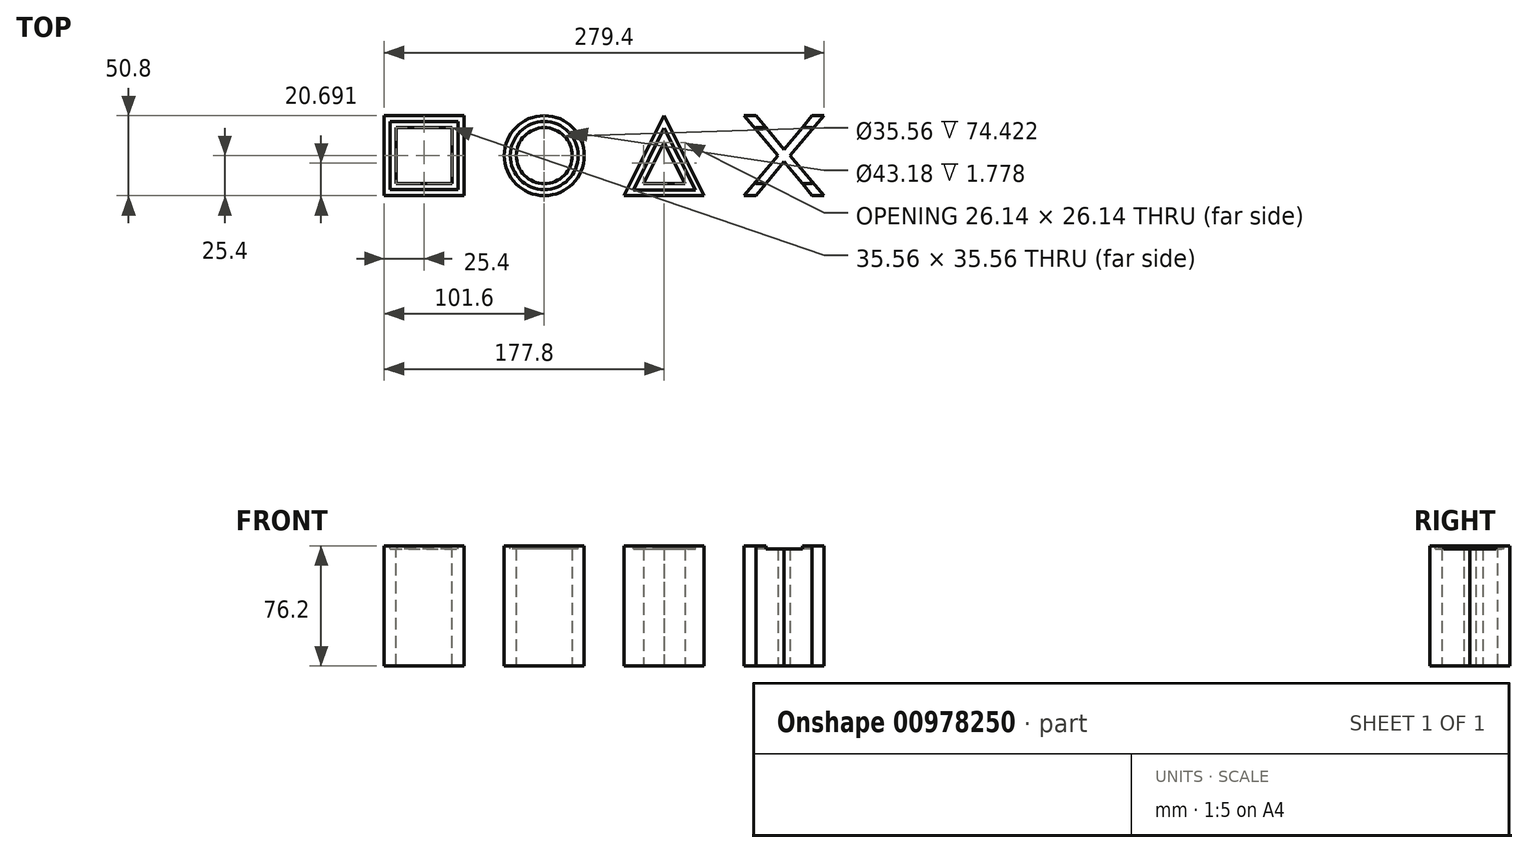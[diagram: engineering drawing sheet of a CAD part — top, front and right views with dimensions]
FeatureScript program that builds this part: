
annotation { "Feature Type Name" : "Feature", "Feature Type Description" : "" }
export const myFeature = defineFeature(function(context is Context, id is Id, definition is map)
    precondition{}
    {
        {
            var Q0;
            Q0=qCreatedBy(makeId("Top.planeOp"),FACE);
            var sketch = newSketch(context, id + "F0", { "sketchPlane" : qUnion([Q0])});
            skLineSegment(sketch, "E0.bottom", {"start": v(139.7, -25.4) * mm, "end": v(-139.7, -25.4) * mm});
            skLineSegment(sketch, "E0.top", {"start": v(139.7, 25.4) * mm, "end": v(-139.7, 25.4) * mm});
            skLineSegment(sketch, "E0.left", {"start": v(139.7, -25.4) * mm, "end": v(139.7, 25.4) * mm});
            skLineSegment(sketch, "E0.right", {"start": v(-139.7, -25.4) * mm, "end": v(-139.7, 25.4) * mm});
            skPoint(sketch, "E0.middle", {"position": v(0, 0) * mm});
            skSolve(sketch);
        }
        {
            var Q0;
            Q0=qSketchRegion(id+"F0",true);
            extrude(context, id + "F1", {"entities" : qUnion([Q0]), "oppositeDirection" : true, "depth" : 25.4 * mm, "offsetDistance" : 25.4 * mm});
        }
        {
            var Q0;
            Q0=makeQuery(id+"F1.opExtrude","CAP_FACE",FACE,{"disambiguationData":[OSD([sQuery(id+"F0.wireOp",EDGE,"E0.bottom"),sQuery(id+"F0.wireOp",EDGE,"E0.top"),sQuery(id+"F0.wireOp",EDGE,"E0.left"),sQuery(id+"F0.wireOp",EDGE,"E0.right")])],"isStart":true});
            var sketch = newSketch(context, id + "F2", { "sketchPlane" : qUnion([Q0])});
            skLineSegment(sketch, "E1.bottom", {"start": v(-139.7, 25.4) * mm, "end": v(-88.9, 25.4) * mm});
            skLineSegment(sketch, "E1.top", {"start": v(-139.7, -25.4) * mm, "end": v(-88.9, -25.4) * mm});
            skLineSegment(sketch, "E1.left", {"start": v(-139.7, 25.4) * mm, "end": v(-139.7, -25.4) * mm});
            skLineSegment(sketch, "E1.right", {"start": v(-88.9, 25.4) * mm, "end": v(-88.9, -25.4) * mm});
            skSolve(sketch);
        }
        {
            var Q0;
            Q0=qSketchRegion(id+"F2",true);
            extrude(context, id + "F3", {"entities" : qUnion([Q0]), "depth" : 127 * mm, "offsetDistance" : 25.4 * mm});
        }
        {
            var Q0;
            Q0=makeQuery(id+"F3.opExtrude","CAP_FACE",FACE,{"disambiguationData":[OSD([sQuery(id+"F2.wireOp",EDGE,"E1.bottom"),sQuery(id+"F2.wireOp",EDGE,"E1.top"),sQuery(id+"F2.wireOp",EDGE,"E1.left"),sQuery(id+"F2.wireOp",EDGE,"E1.right")])],"isStart":false});
            var sketch = newSketch(context, id + "F4", { "sketchPlane" : qUnion([Q0])});
            skLineSegment(sketch, "E2.bottom", {"start": v(-132.08, -17.78) * mm, "end": v(-96.52, -17.78) * mm});
            skLineSegment(sketch, "E2.top", {"start": v(-132.08, 17.78) * mm, "end": v(-96.52, 17.78) * mm});
            skLineSegment(sketch, "E2.left", {"start": v(-132.08, -17.78) * mm, "end": v(-132.08, 17.78) * mm});
            skLineSegment(sketch, "E2.right", {"start": v(-96.52, -17.78) * mm, "end": v(-96.52, 17.78) * mm});
            skPoint(sketch, "E2.middle", {"position": v(-114.3, 0) * mm});
            skPoint(sketch, "E2.middle.positionSnap0", {"position": v(-88.9, 0) * mm});
            skPoint(sketch, "E2.middle.positionSnap1", {"position": v(-114.3, 25.4) * mm});
            skPoint(sketch, "E2.centerSnap0", {"position": v(-88.9, 0) * mm});
            skPoint(sketch, "E2.centerSnap1", {"position": v(-114.3, 25.4) * mm});
            skSolve(sketch);
        }
        {
            var Q0;
            Q0=qSketchRegion(id+"F4",true);
            extrude(context, id + "F5", {"entities" : qUnion([Q0]), "operationType" : NewBodyOperationType.REMOVE, "oppositeDirection" : true, "depth" : 127 * mm, "offsetDistance" : 25.4 * mm});
        }
        {
            var Q0;
            Q0=makeQuery(id+"F1.opExtrude","CAP_FACE",FACE,{"disambiguationData":[OSD([sQuery(id+"F0.wireOp",EDGE,"E0.bottom"),sQuery(id+"F0.wireOp",EDGE,"E0.top"),sQuery(id+"F0.wireOp",EDGE,"E0.left"),sQuery(id+"F0.wireOp",EDGE,"E0.right")])],"isStart":true});
            var sketch = newSketch(context, id + "F6", { "sketchPlane" : qUnion([Q0])});
            skCircle(sketch, "E3", {"center": v(-38.1, 0) * mm, "radius": 25.4 * mm});
            skCircle(sketch, "E4", {"center": v(-38.1, 0) * mm, "radius": 17.78 * mm});
            skSolve(sketch);
        }
        {
            var Q0;
            Q0=qSketchRegion(id+"F6",true);
            extrude(context, id + "F7", {"entities" : qUnion([Q0]), "depth" : 127 * mm, "offsetDistance" : 25.4 * mm});
        }
        {
            var Q0;
            Q0=makeQuery(id+"F1.opExtrude","CAP_FACE",FACE,{"disambiguationData":[OSD([sQuery(id+"F0.wireOp",EDGE,"E0.bottom"),sQuery(id+"F0.wireOp",EDGE,"E0.top"),sQuery(id+"F0.wireOp",EDGE,"E0.left"),sQuery(id+"F0.wireOp",EDGE,"E0.right")])],"isStart":true});
            var sketch = newSketch(context, id + "F8", { "sketchPlane" : qUnion([Q0])});
            skLineSegment(sketch, "E5.bottom", {"start": v(12.7, -25.4) * mm, "end": v(63.5, -25.4) * mm});
            skLineSegment(sketch, "E6", {"start": v(38.1, 25.4) * mm, "end": v(12.7, -25.4) * mm});
            skLineSegment(sketch, "E7", {"start": v(38.1, 25.4) * mm, "end": v(63.5, -25.4) * mm});
            skLineSegment(sketch, "E8", {"start": v(38.1, 8.36) * mm, "end": v(25.03, -17.78) * mm});
            skLineSegment(sketch, "E9", {"start": v(25.03, -17.78) * mm, "end": v(51.17, -17.78) * mm});
            skLineSegment(sketch, "E10", {"start": v(51.17, -17.78) * mm, "end": v(38.1, 8.36) * mm});
            skSolve(sketch);
        }
        {
            var Q0;
            Q0=qSketchRegion(id+"F8",true);
            extrude(context, id + "F9", {"entities" : qUnion([Q0]), "depth" : 127 * mm, "offsetDistance" : 25.4 * mm});
        }
        {
            var Q0;
            Q0=makeQuery(id+"F1.opExtrude","CAP_FACE",FACE,{"disambiguationData":[OSD([sQuery(id+"F0.wireOp",EDGE,"E0.bottom"),sQuery(id+"F0.wireOp",EDGE,"E0.top"),sQuery(id+"F0.wireOp",EDGE,"E0.left"),sQuery(id+"F0.wireOp",EDGE,"E0.right")])],"isStart":true});
            var sketch = newSketch(context, id + "F10", { "sketchPlane" : qUnion([Q0])});
            skPoint(sketch, "E11.middle", {"position": v(114.3, 0) * mm});
            skLineSegment(sketch, "E12", {"start": v(88.9, -25.4) * mm, "end": v(96.52, -25.4) * mm});
            skLineSegment(sketch, "E13", {"start": v(96.52, -25.4) * mm, "end": v(114.3, -3.81) * mm});
            skLineSegment(sketch, "E14", {"start": v(88.9, -25.4) * mm, "end": v(110.49, 0) * mm});
            skLineSegment(sketch, "E15", {"start": v(110.49, 0) * mm, "end": v(88.9, 25.4) * mm});
            skLineSegment(sketch, "E16", {"start": v(88.9, 25.4) * mm, "end": v(96.52, 25.4) * mm});
            skLineSegment(sketch, "E17", {"start": v(96.52, 25.4) * mm, "end": v(114.3, 3.8) * mm});
            skLineSegment(sketch, "E18", {"start": v(139.7, 25.4) * mm, "end": v(118.11, 0) * mm});
            skLineSegment(sketch, "E19", {"start": v(118.1, 0) * mm, "end": v(139.7, -25.4) * mm});
            skLineSegment(sketch, "E20", {"start": v(139.7, 25.4) * mm, "end": v(132.08, 25.4) * mm});
            skLineSegment(sketch, "E21", {"start": v(132.08, 25.4) * mm, "end": v(114.3, 3.8) * mm});
            skLineSegment(sketch, "E22", {"start": v(139.7, -25.4) * mm, "end": v(132.08, -25.4) * mm});
            skLineSegment(sketch, "E23", {"start": v(132.08, -25.4) * mm, "end": v(114.3, -3.81) * mm});
            skSolve(sketch);
        }
        {
            var Q0;
            Q0=qSketchRegion(id+"F10",true);
            extrude(context, id + "F11", {"entities" : qUnion([Q0]), "depth" : 127 * mm, "offsetDistance" : 25.4 * mm});
        }
        {
            var Q0;
            Q0=makeQuery(id+"F1.opExtrude","CAP_FACE",FACE,{"disambiguationData":[OSD([sQuery(id+"F0.wireOp",EDGE,"E0.bottom"),sQuery(id+"F0.wireOp",EDGE,"E0.top"),sQuery(id+"F0.wireOp",EDGE,"E0.left"),sQuery(id+"F0.wireOp",EDGE,"E0.right")])],"isStart":false});
            var sketch = newSketch(context, id + "F12", { "sketchPlane" : qUnion([Q0])});
            skLineSegment(sketch, "E24.bottom", {"start": v(-151.26, 33.82) * mm, "end": v(154.08, 33.82) * mm});
            skLineSegment(sketch, "E24.top", {"start": v(-151.26, -31.19) * mm, "end": v(154.08, -31.19) * mm});
            skLineSegment(sketch, "E24.left", {"start": v(-151.26, 33.82) * mm, "end": v(-151.26, -31.19) * mm});
            skLineSegment(sketch, "E24.right", {"start": v(154.08, 33.82) * mm, "end": v(154.08, -31.19) * mm});
            skSolve(sketch);
        }
        {
            var Q0;
            Q0 = qSketchRegion(id + "F12", true);
            extrude(context, id + "F13", {"entities" : qUnion([Q0]), "operationType" : NewBodyOperationType.REMOVE, "oppositeDirection" : true, "depth" : 76.2 * mm, "offsetDistance" : 25.4 * mm});
        }
        {
            var Q0;
            Q0=makeQuery(id+"F3.opExtrude","CAP_FACE",FACE,{"disambiguationData":[OSD([sQuery(id+"F2.wireOp",EDGE,"E1.bottom"),sQuery(id+"F2.wireOp",EDGE,"E1.top"),sQuery(id+"F2.wireOp",EDGE,"E1.left"),sQuery(id+"F2.wireOp",EDGE,"E1.right")])],"isStart":false});
            var sketch = newSketch(context, id + "F14", { "sketchPlane" : qUnion([Q0])});
            skLineSegment(sketch, "E25.bottom", {"start": v(-135.9, -21.6) * mm, "end": v(-92.71, -21.6) * mm});
            skLineSegment(sketch, "E25.top", {"start": v(-135.9, 21.59) * mm, "end": v(-92.71, 21.59) * mm});
            skLineSegment(sketch, "E25.left", {"start": v(-135.9, -21.6) * mm, "end": v(-135.9, 21.59) * mm});
            skLineSegment(sketch, "E25.right", {"start": v(-92.71, -21.6) * mm, "end": v(-92.71, 21.59) * mm});
            skPoint(sketch, "E25.middle", {"position": v(-114.3, 0) * mm});
            skPoint(sketch, "E25.middle.positionSnap0", {"position": v(-114.3, 17.78) * mm});
            skPoint(sketch, "E25.middle.positionSnap1", {"position": v(-132.08, 0) * mm});
            skPoint(sketch, "E25.centerSnap0", {"position": v(-114.3, 17.78) * mm});
            skPoint(sketch, "E25.centerSnap1", {"position": v(-132.08, 0) * mm});
            skSolve(sketch);
        }
        {
            var Q0;
            Q0 = qSketchRegion(id + "F14", true);
            extrude(context, id + "F15", {"entities" : qUnion([Q0]), "operationType" : NewBodyOperationType.REMOVE, "oppositeDirection" : true, "depth" : 1.78 * mm, "offsetDistance" : 25.4 * mm});
        }
        {
            var Q0;
            Q0=makeQuery(id+"F7.opExtrude","CAP_FACE",FACE,{"disambiguationData":[OSD([sQuery(id+"F6.wireOp",EDGE,"E3"),sQuery(id+"F6.wireOp",EDGE,"E4")])],"isStart":false});
            var sketch = newSketch(context, id + "F16", { "sketchPlane" : qUnion([Q0])});
            skCircle(sketch, "E26", {"center": v(-38.1, 0) * mm, "radius": 21.59 * mm});
            skSolve(sketch);
        }
        {
            var Q0;
            Q0 = qSketchRegion(id + "F16", true);
            extrude(context, id + "F17", {"entities" : qUnion([Q0]), "operationType" : NewBodyOperationType.REMOVE, "oppositeDirection" : true, "depth" : 1.78 * mm, "offsetDistance" : 25.4 * mm});
        }
        {
            var Q0;
            Q0=makeQuery(id+"F9.opExtrude","CAP_FACE",FACE,{"disambiguationData":[OSD([sQuery(id+"F8.wireOp",EDGE,"E5.bottom"),sQuery(id+"F8.wireOp",EDGE,"E6"),sQuery(id+"F8.wireOp",EDGE,"E7"),sQuery(id+"F8.wireOp",EDGE,"E8"),sQuery(id+"F8.wireOp",EDGE,"E9"),sQuery(id+"F8.wireOp",EDGE,"E10")])],"isStart":false});
            var sketch = newSketch(context, id + "F18", { "sketchPlane" : qUnion([Q0])});
            skLineSegment(sketch, "E27", {"start": v(38.1, 17.4) * mm, "end": v(18.49, -21.82) * mm});
            skLineSegment(sketch, "E28", {"start": v(18.49, -21.82) * mm, "end": v(58.12, -21.82) * mm});
            skLineSegment(sketch, "E29", {"start": v(58.12, -21.82) * mm, "end": v(38.1, 17.4) * mm});
            skSolve(sketch);
        }
        {
            var Q0;
            Q0 = qSketchRegion(id + "F18", true);
            extrude(context, id + "F19", {"entities" : qUnion([Q0]), "operationType" : NewBodyOperationType.REMOVE, "oppositeDirection" : true, "depth" : 1.78 * mm, "offsetDistance" : 25.4 * mm});
        }
        {
            var Q0;
            Q0=makeQuery(id+"F11.opExtrude","CAP_FACE",FACE,{"disambiguationData":[OSD([sQuery(id+"F10.wireOp",EDGE,"E12"),sQuery(id+"F10.wireOp",EDGE,"E13"),sQuery(id+"F10.wireOp",EDGE,"E14"),sQuery(id+"F10.wireOp",EDGE,"E15"),sQuery(id+"F10.wireOp",EDGE,"E16"),sQuery(id+"F10.wireOp",EDGE,"E17"),sQuery(id+"F10.wireOp",EDGE,"E18"),sQuery(id+"F10.wireOp",EDGE,"E19"),sQuery(id+"F10.wireOp",EDGE,"E20"),sQuery(id+"F10.wireOp",EDGE,"E21"),sQuery(id+"F10.wireOp",EDGE,"E22"),sQuery(id+"F10.wireOp",EDGE,"E23")])],"isStart":false});
            var sketch = newSketch(context, id + "F20", { "sketchPlane" : qUnion([Q0])});
            skLineSegment(sketch, "E30.bottom", {"start": v(132.08, -17.78) * mm, "end": v(96.52, -17.78) * mm});
            skLineSegment(sketch, "E30.top", {"start": v(132.08, 17.78) * mm, "end": v(96.52, 17.78) * mm});
            skLineSegment(sketch, "E30.left", {"start": v(132.08, -17.78) * mm, "end": v(132.08, 17.78) * mm});
            skLineSegment(sketch, "E30.right", {"start": v(96.52, -17.78) * mm, "end": v(96.52, 17.78) * mm});
            skPoint(sketch, "E30.middle", {"position": v(114.3, 0) * mm});
            skSolve(sketch);
        }
        {
            var Q0;
            Q0 = qSketchRegion(id + "F20", true);
            extrude(context, id + "F21", {"entities" : qUnion([Q0]), "operationType" : NewBodyOperationType.REMOVE, "oppositeDirection" : true, "depth" : 1.78 * mm, "offsetDistance" : 25.4 * mm});
        }
    });
